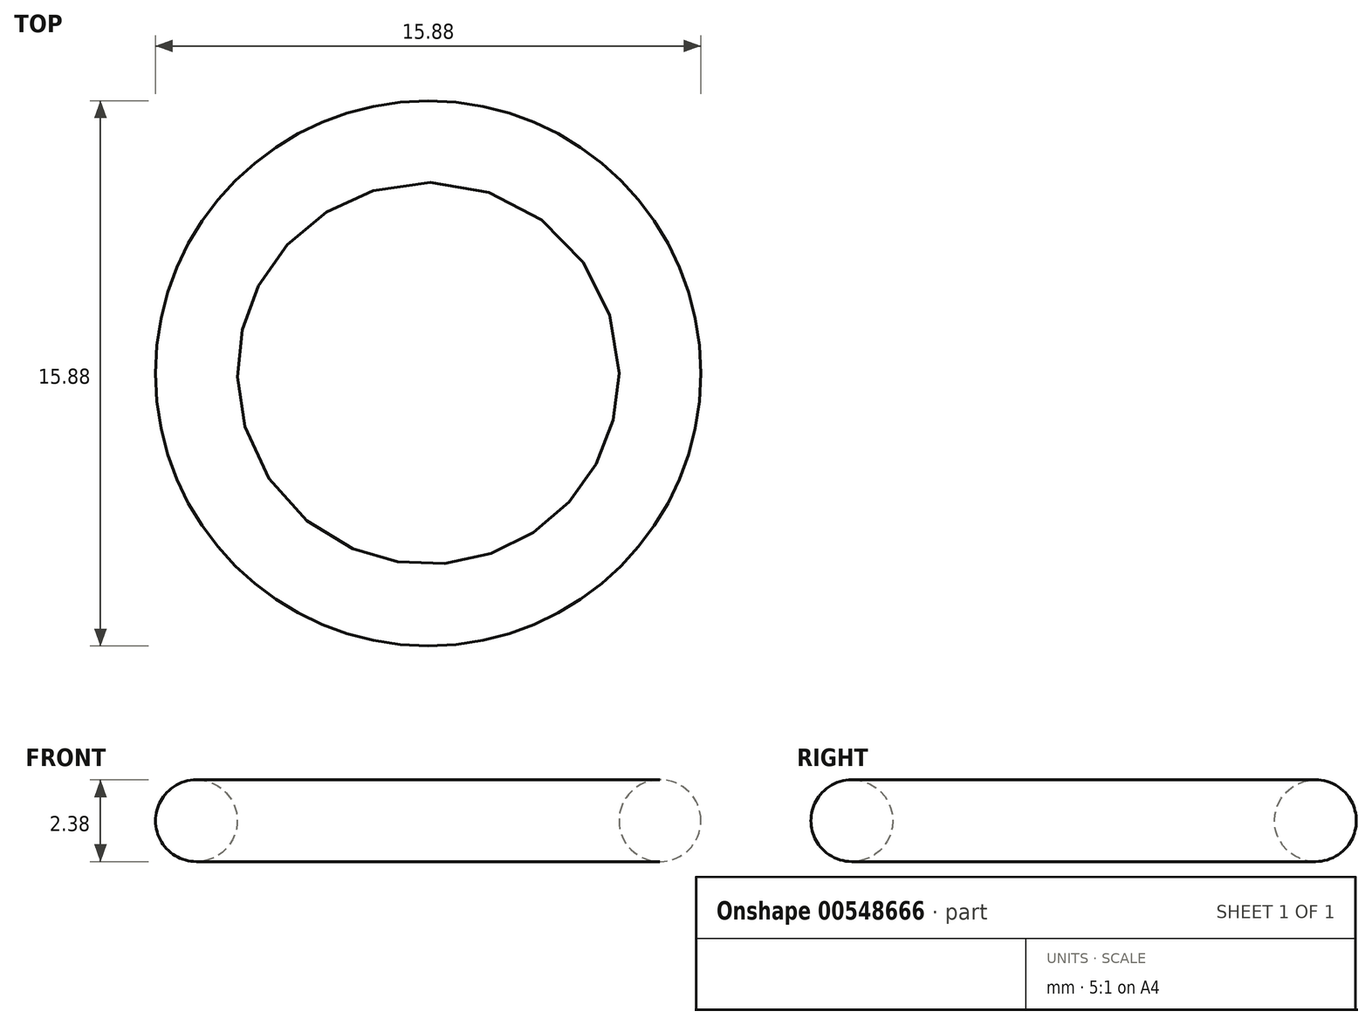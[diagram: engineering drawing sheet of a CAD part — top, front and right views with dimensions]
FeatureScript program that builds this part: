
annotation { "Feature Type Name" : "Feature", "Feature Type Description" : "" }
export const myFeature = defineFeature(function(context is Context, id is Id, definition is map)
    precondition{}
    {
        {
            var Q0;
            Q0=qCreatedBy(makeId("Front.planeOp"),FACE);
            var sketch = newSketch(context, id + "F0", { "sketchPlane" : qUnion([Q0])});
            skCircle(sketch, "E0", {"center": v(-6.75, 0) * mm, "radius": 1.2 * mm});
            skPoint(sketch, "E1", {"position": v(-7.94, 0) * mm});
            skLineSegment(sketch, "E2", {"start": v(0, 19.53) * mm, "end": v(0, -8.36) * mm, "construction": true});
            skSolve(sketch);
        }
        {
            var Q0;
            Q0 = qSketchRegion(id + "F0", true);
            var Q1;
            Q1=sQuery(id+"F0.wireOp",EDGE,"E2");
            revolve(context, id + "F1", {"entities" : qUnion([Q0]), "axis" : qUnion([Q1]), "revolveType" : RevolveType.FULL});
        }
    });
